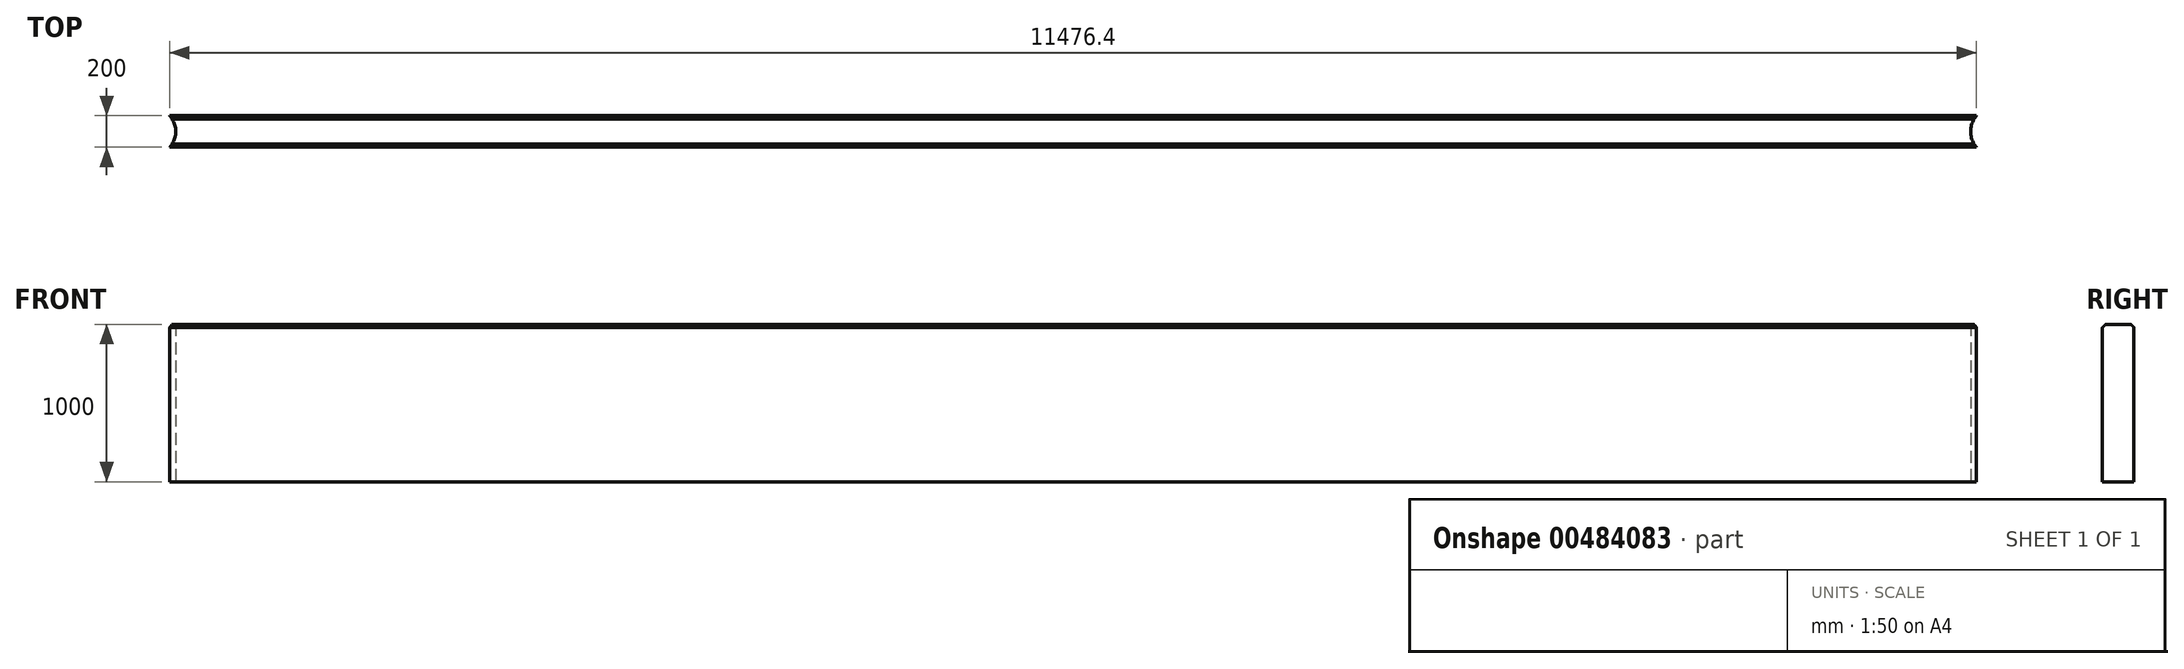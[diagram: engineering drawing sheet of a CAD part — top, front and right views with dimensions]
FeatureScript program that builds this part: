
annotation { "Feature Type Name" : "Feature", "Feature Type Description" : "" }
export const myFeature = defineFeature(function(context is Context, id is Id, definition is map)
    precondition{}
    {
        {
            var Q0;
            Q0=qCreatedBy(makeId("Top.planeOp"),FACE);
            var sketch = newSketch(context, id + "F0", { "sketchPlane" : qUnion([Q0])});
            skArc(sketch, "E0", {"start": v(-111.8, 100) * mm, "mid": v(-149.46, 0) * mm, "end": v(-111.8, -100) * mm});
            skArc(sketch, "E1", {"start": v(-11588.2, -100) * mm, "mid": v(-11548.83, 0) * mm, "end": v(-11588.2, 100) * mm});
            skLineSegment(sketch, "E2", {"start": v(-111.8, 100) * mm, "end": v(-11588.2, 100) * mm});
            skLineSegment(sketch, "E3", {"start": v(-111.8, -100) * mm, "end": v(-11588.2, -100) * mm});
            skSolve(sketch);
        }
        {
            var Q0;
            Q0=makeQuery(id+"F0.imprint","IMPRINT",FACE,{"disambiguationData":[TD([[makeQuery(id+"F0.imprint","IMPRINT",EDGE,{"derivedFrom":sQuery(id+"F0.wireOp",EDGE,"E0")}),-1.0]])]});
            extrude(context, id + "F1", {"entities" : qUnion([Q0]), "depth" : 1000 * mm});
        }
        {
            var Q0;
            Q0=makeQuery(id+"F1.opExtrude","CAP_EDGE",EDGE,{"disambiguationData":[OSD([sQuery(id+"F0.wireOp",EDGE,"E3")])],"isStart":false});
            chamfer(context, id + "F2", {"entities" : qUnion([Q0]), "width" : 20 * mm, "tangentPropagation" : true});
        }
        {
            var Q0;
            Q0=makeQuery(id+"F1.opExtrude","CAP_EDGE",EDGE,{"disambiguationData":[OSD([sQuery(id+"F0.wireOp",EDGE,"E2")])],"isStart":false});
            chamfer(context, id + "F3", {"entities" : qUnion([Q0]), "width" : 20 * mm, "tangentPropagation" : true});
        }
    });
